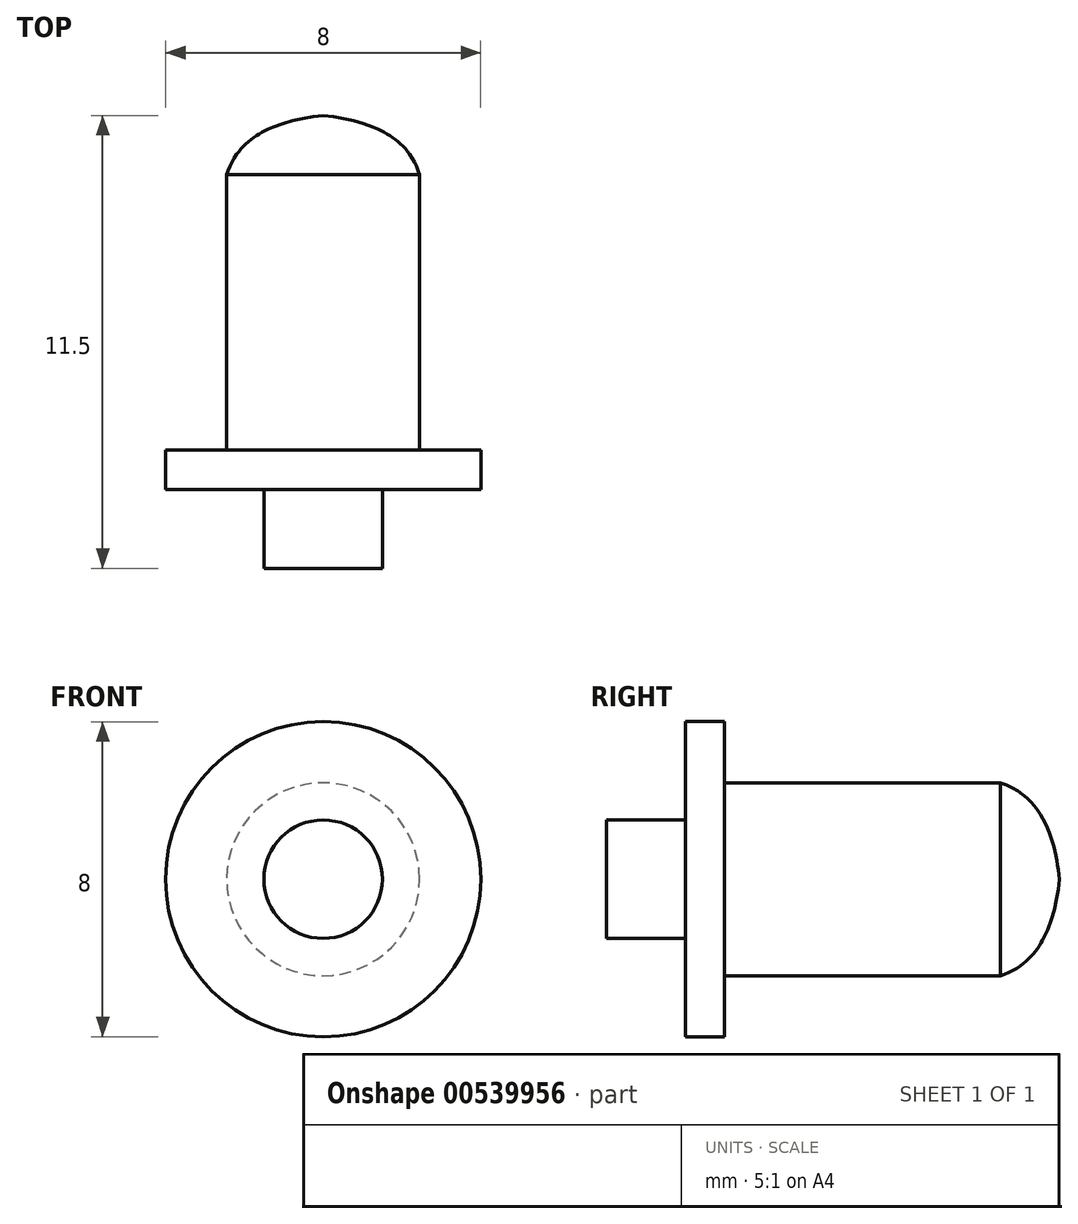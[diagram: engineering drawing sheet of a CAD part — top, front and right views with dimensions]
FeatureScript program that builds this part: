
annotation { "Feature Type Name" : "Feature", "Feature Type Description" : "" }
export const myFeature = defineFeature(function(context is Context, id is Id, definition is map)
    precondition{}
    {
        {
            var Q0;
            Q0=qCreatedBy(makeId("Right.planeOp"),FACE);
            var sketch = newSketch(context, id + "F0", { "sketchPlane" : qUnion([Q0])});
            skLineSegment(sketch, "E0", {"start": v(-2, 0) * mm, "end": v(-2, 1.5) * mm});
            skLineSegment(sketch, "E1", {"start": v(-2, 1.5) * mm, "end": v(0, 1.5) * mm});
            skLineSegment(sketch, "E2", {"start": v(0, 1.5) * mm, "end": v(0, 4) * mm});
            skLineSegment(sketch, "E3", {"start": v(0, 4) * mm, "end": v(1, 4) * mm});
            skPoint(sketch, "E4.endSnap0", {"position": v(-1, 1.5) * mm});
            skLineSegment(sketch, "E5", {"start": v(8, 2.45) * mm, "end": v(1, 2.45) * mm});
            skLineSegment(sketch, "E6", {"start": v(1, 2.45) * mm, "end": v(1, 4) * mm});
            skPoint(sketch, "E7.2.internal.orphan", {"position": v(10.2, -6.36) * mm});
            skLineSegment(sketch, "E8", {"start": v(9.5, 0) * mm, "end": v(-2, 0) * mm});
            skFitSpline(sketch, "E9.trimOffspring", {"points": [v(8.2, 2.45) * mm, v(10.2, 0) * mm, v(10.2, -6.36) * mm, v(10.2, -5.94) * mm], "startDerivative": vector(6.86, -4.03) * mm, "endDerivative": vector(0.19, 5.18) * mm});
            skPoint(sketch, "E10.visualSharp", {"position": v(9.5, 0.26) * mm});
            skFitSpline(sketch, "E11", {"points": [v(8, 2.45) * mm, v(9.2, 1.27) * mm, v(9.5, 0) * mm], "startDerivative": vector(3.92, -1.24) * mm, "endDerivative": vector(0.24, -2.83) * mm});
            skSolve(sketch);
        }
        {
            var Q0;
            Q0 = qSketchRegion(id + "F0", true);
            var Q1;
            Q1=sQuery(id+"F0.wireOp",EDGE,"E8");
            revolve(context, id + "F1", {"surfaceOperationType" : NewSurfaceOperationType.NEW, "entities" : qUnion([Q0]), "axis" : qUnion([Q1]), "revolveType" : RevolveType.FULL});
        }
    });
